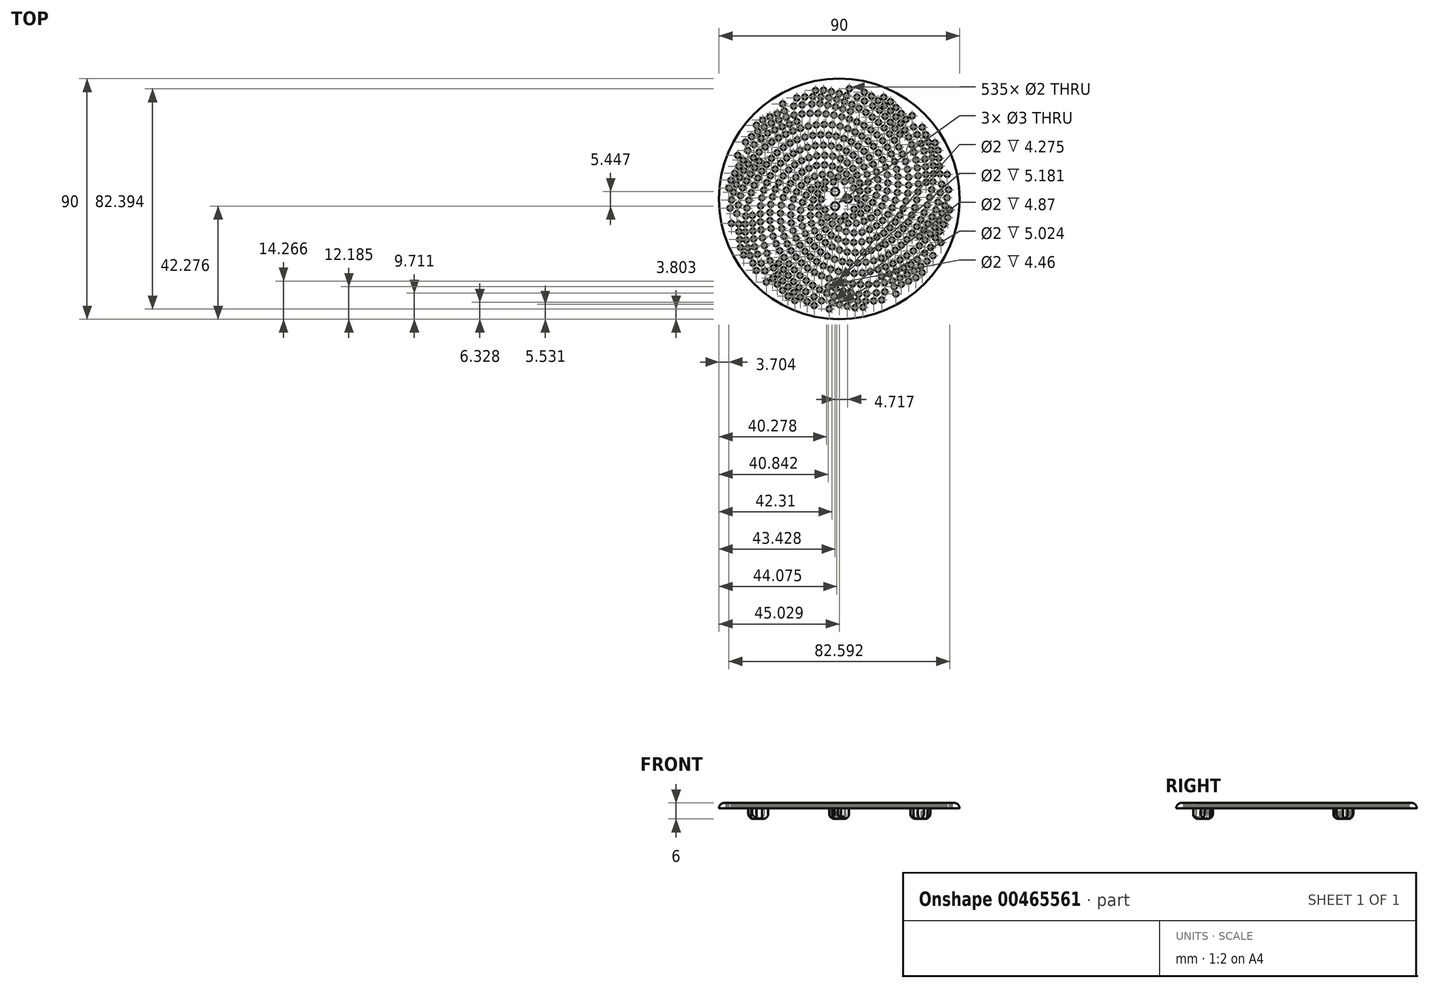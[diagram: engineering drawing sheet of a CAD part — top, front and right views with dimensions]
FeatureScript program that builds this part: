
annotation { "Feature Type Name" : "Feature", "Feature Type Description" : "" }
export const myFeature = defineFeature(function(context is Context, id is Id, definition is map)
    precondition{}
    {
        {
            var Q0;
            Q0=qCreatedBy(makeId("Top.planeOp"),FACE);
            var sketch = newSketch(context, id + "F0", { "sketchPlane" : qUnion([Q0])});
            skCircle(sketch, "E0", {"center": v(0, 0) * mm, "radius": 45 * mm});
            skSolve(sketch);
        }
        {
            var Q0;
            Q0=makeQuery(id+"F0.imprint","IMPRINT",FACE,{"disambiguationData":[TD([[makeQuery(id+"F0.imprint","IMPRINT",EDGE,{"derivedFrom":sQuery(id+"F0.wireOp",EDGE,"E0")}),1.0]])]});
            extrude(context, id + "F1", {"entities" : qUnion([Q0]), "depth" : 2 * mm});
        }
        {
            var Q0;
            Q0=makeQuery(id+"F1.opExtrude","CAP_FACE",FACE,{"disambiguationData":[OSD([sQuery(id+"F0.wireOp",EDGE,"E0")])],"isStart":true});
            var sketch = newSketch(context, id + "F2", { "sketchPlane" : qUnion([Q0])});
            skCircle(sketch, "E1", {"center": v(0, 35) * mm, "radius": 5.25 * mm});
            skCircle(sketch, "E2.1.0", {"center": v(-30.31, -17.5) * mm, "radius": 5.25 * mm});
            skCircle(sketch, "E2.2.0", {"center": v(30.31, -17.5) * mm, "radius": 5.25 * mm});
            skPoint(sketch, "E2.center", {"position": v(0, 0) * mm});
            skSolve(sketch);
        }
        {
            var Q0;
            Q0 = qSketchRegion(id + "F2", true);
            extrude(context, id + "F3", {"entities" : qUnion([Q0]), "operationType" : NewBodyOperationType.REMOVE, "oppositeDirection" : true, "depth" : 1 * mm});
        }
        {
            var Q0;
            Q0=makeQuery(id+"F3.boolean.opBoolean","COPY",FACE,{"derivedFrom":makeQuery(id+"F3.opExtrude","CAP_FACE",FACE,{"disambiguationData":[OSD([sQuery(id+"F2.wireOp",EDGE,"E1")])],"isStart":false})});
            var sketch = newSketch(context, id + "F4", { "sketchPlane" : qUnion([Q0])});
            skCircle(sketch, "E3", {"center": v(0, 35) * mm, "radius": 3.75 * mm});
            skCircle(sketch, "E4.1.0", {"center": v(-30.31, -17.5) * mm, "radius": 3.75 * mm});
            skCircle(sketch, "E4.2.0", {"center": v(30.31, -17.5) * mm, "radius": 3.75 * mm});
            skPoint(sketch, "E4.center", {"position": v(0, 0) * mm});
            skSolve(sketch);
        }
        {
            var Q0;
            Q0=makeQuery(id+"F4.imprint","IMPRINT",FACE,{"disambiguationData":[TD([[makeQuery(id+"F4.imprint","IMPRINT",EDGE,{"derivedFrom":sQuery(id+"F4.wireOp",EDGE,"E3")}),1.0]])]});
            var Q1;
            Q1=makeQuery(id+"F4.imprint","IMPRINT",FACE,{"disambiguationData":[TD([[makeQuery(id+"F4.imprint","IMPRINT",EDGE,{"derivedFrom":sQuery(id+"F4.wireOp",EDGE,"E4.2.0")}),1.0]])]});
            var Q2;
            Q2=makeQuery(id+"F4.imprint","IMPRINT",FACE,{"disambiguationData":[TD([[makeQuery(id+"F4.imprint","IMPRINT",EDGE,{"derivedFrom":sQuery(id+"F4.wireOp",EDGE,"E4.1.0")}),1.0]])]});
            extrude(context, id + "F5", {"entities" : qUnion([Q0, Q1, Q2]), "operationType" : NewBodyOperationType.ADD, "depth" : 5 * mm});
        }
        {
            var Q0;
            Q0=makeQuery(id+"F5.opExtrude","CAP_FACE",FACE,{"disambiguationData":[OSD([sQuery(id+"F4.wireOp",EDGE,"E4.1.0")])],"isStart":false});
            var Q1;
            Q1=makeQuery(id+"F5.opExtrude","CAP_FACE",FACE,{"disambiguationData":[OSD([sQuery(id+"F4.wireOp",EDGE,"E3")])],"isStart":false});
            var Q2;
            Q2=makeQuery(id+"F5.opExtrude","CAP_FACE",FACE,{"disambiguationData":[OSD([sQuery(id+"F4.wireOp",EDGE,"E4.2.0")])],"isStart":false});
            fillet(context, id + "F6", {"entities" : qUnion([Q0, Q1, Q2]), "radius" : 2 * mm, "tangentPropagation" : true, "allowEdgeOverflow" : false});
        }
        {
            var Q0;
            Q0=makeQuery(id+"F1.opExtrude","CAP_EDGE",EDGE,{"disambiguationData":[OSD([sQuery(id+"F0.wireOp",EDGE,"E0")])],"isStart":false});
            fillet(context, id + "F7", {"entities" : qUnion([Q0]), "radius" : 2 * mm, "tangentPropagation" : true, "allowEdgeOverflow" : false});
        }
        {
            var Q0;
            Q0=makeQuery(id+"F1.opExtrude","CAP_FACE",FACE,{"disambiguationData":[OSD([sQuery(id+"F0.wireOp",EDGE,"E0")])],"isStart":false});
            var sketch = newSketch(context, id + "F8", { "sketchPlane" : qUnion([Q0])});
            skCircle(sketch, "E5", {"center": v(0, 0) * mm, "radius": 4.62 * mm, "construction": true});
            skFitSpline(sketch, "E6", {"points": [v(-41.37, -9.4) * mm, v(-31.79, 15.74) * mm, v(-5.3, 27.85) * mm, v(12.82, 19.64) * mm, v(18.16, 6) * mm, v(13.17, -6.11) * mm, v(3.17, -9.08) * mm, v(-2.43, -5.86) * mm, v(-4.4, -1.42) * mm], "startDerivative": vector(4.04, 165.6) * mm, "endDerivative": vector(-19.47, 63.53) * mm, "construction": true});
            skCircle(sketch, "E7", {"center": v(-40.85, -3.42) * mm, "radius": 1 * mm});
            skCircle(sketch, "E8", {"center": v(-37.22, 8.02) * mm, "radius": 1 * mm});
            skCircle(sketch, "E9", {"center": v(-39.48, 2.47) * mm, "radius": 1 * mm});
            skCircle(sketch, "E10", {"center": v(-38.47, 5.3) * mm, "radius": 1 * mm});
            skCircle(sketch, "E11", {"center": v(-40.27, -0.42) * mm, "radius": 1 * mm});
            skCircle(sketch, "E12", {"center": v(-35.74, 10.63) * mm, "radius": 1 * mm});
            skCircle(sketch, "E13", {"center": v(-34.03, 13.1) * mm, "radius": 1 * mm});
            skCircle(sketch, "E14", {"center": v(-32.1, 15.4) * mm, "radius": 1 * mm});
            skCircle(sketch, "E15", {"center": v(-22.72, 22.8) * mm, "radius": 1 * mm});
            skCircle(sketch, "E16", {"center": v(-27.7, 19.46) * mm, "radius": 1 * mm});
            skCircle(sketch, "E17", {"center": v(-25.27, 21.22) * mm, "radius": 1 * mm});
            skCircle(sketch, "E18", {"center": v(-29.98, 17.52) * mm, "radius": 1 * mm});
            skCircle(sketch, "E19", {"center": v(-20.06, 24.2) * mm, "radius": 1 * mm});
            skCircle(sketch, "E20", {"center": v(-17.32, 25.4) * mm, "radius": 1 * mm});
            skCircle(sketch, "E21", {"center": v(-14.49, 26.4) * mm, "radius": 1 * mm});
            skCircle(sketch, "E22", {"center": v(-11.58, 27.16) * mm, "radius": 1 * mm});
            skCircle(sketch, "E23", {"center": v(-8.63, 27.66) * mm, "radius": 1 * mm});
            skCircle(sketch, "E24", {"center": v(-5.63, 27.85) * mm, "radius": 1 * mm});
            skCircle(sketch, "E25", {"center": v(5.91, 25.02) * mm, "radius": 1 * mm});
            skCircle(sketch, "E26", {"center": v(0.31, 27.15) * mm, "radius": 1 * mm});
            skCircle(sketch, "E27", {"center": v(3.18, 26.26) * mm, "radius": 1 * mm});
            skCircle(sketch, "E28", {"center": v(-2.64, 27.69) * mm, "radius": 1 * mm});
            skCircle(sketch, "E29", {"center": v(8.48, 23.46) * mm, "radius": 1 * mm});
            skCircle(sketch, "E30", {"center": v(10.84, 21.61) * mm, "radius": 1 * mm});
            skCircle(sketch, "E31", {"center": v(12.82, 19.64) * mm, "radius": 1 * mm});
            skCircle(sketch, "E32", {"center": v(14.67, 17.28) * mm, "radius": 1 * mm});
            skCircle(sketch, "E33", {"center": v(16.18, 14.68) * mm, "radius": 1 * mm});
            skCircle(sketch, "E34", {"center": v(17.29, 11.9) * mm, "radius": 1 * mm});
            skCircle(sketch, "E35", {"center": v(17.16, 0.1) * mm, "radius": 1 * mm});
            skCircle(sketch, "E36", {"center": v(18.16, 6) * mm, "radius": 1 * mm});
            skCircle(sketch, "E37", {"center": v(17.9, 3.02) * mm, "radius": 1 * mm});
            skCircle(sketch, "E38", {"center": v(17.96, 8.97) * mm, "radius": 1 * mm});
            skCircle(sketch, "E39", {"center": v(15.94, -2.63) * mm, "radius": 1 * mm});
            skCircle(sketch, "E40", {"center": v(14.2, -5.08) * mm, "radius": 1 * mm});
            skCircle(sketch, "E41", {"center": v(6.34, -9.1) * mm, "radius": 1 * mm});
            skCircle(sketch, "E42", {"center": v(3.34, -9.1) * mm, "radius": 1 * mm});
            skCircle(sketch, "E43", {"center": v(9.26, -8.4) * mm, "radius": 1 * mm});
            skCircle(sketch, "E44", {"center": v(11.94, -7.05) * mm, "radius": 1 * mm});
            skCircle(sketch, "E45", {"center": v(0.47, -8.23) * mm, "radius": 1 * mm});
            skCircle(sketch, "E46", {"center": v(-1.94, -6.45) * mm, "radius": 1 * mm});
            skCircle(sketch, "E47.1.1", {"center": v(13.8, 1.32) * mm, "radius": 1 * mm});
            skCircle(sketch, "E47.1.2", {"center": v(-9.92, 23.72) * mm, "radius": 1 * mm});
            skCircle(sketch, "E47.1.3", {"center": v(10.48, -3.64) * mm, "radius": 1 * mm});
            skCircle(sketch, "E47.1.4", {"center": v(7, 19.79) * mm, "radius": 1 * mm});
            skCircle(sketch, "E47.1.5", {"center": v(9.25, 17.82) * mm, "radius": 1 * mm});
            skCircle(sketch, "E47.1.6", {"center": v(-25.34, 15.17) * mm, "radius": 1 * mm});
            skCircle(sketch, "E47.1.7", {"center": v(-34.55, -3.45) * mm, "radius": 1 * mm});
            skCircle(sketch, "E47.1.8", {"center": v(-30.46, 7.79) * mm, "radius": 1 * mm});
            skCircle(sketch, "E47.1.9", {"center": v(4.46, 21.39) * mm, "radius": 1 * mm});
            skCircle(sketch, "E47.1.10", {"center": v(-28.94, 10.38) * mm, "radius": 1 * mm});
            skCircle(sketch, "E47.1.11", {"center": v(-31.04, -26.78) * mm, "radius": 1 * mm});
            skCircle(sketch, "E47.1.12", {"center": v(-34.83, -15.39) * mm, "radius": 1 * mm});
            skCircle(sketch, "E47.1.13", {"center": v(-33.4, -21.2) * mm, "radius": 1 * mm});
            skCircle(sketch, "E47.1.14", {"center": v(-32.33, -24.01) * mm, "radius": 1 * mm});
            skCircle(sketch, "E47.1.15", {"center": v(13.82, 10.17) * mm, "radius": 1 * mm});
            skCircle(sketch, "E47.1.16", {"center": v(-35.16, -12.4) * mm, "radius": 1 * mm});
            skCircle(sketch, "E47.1.17", {"center": v(-35.23, -9.4) * mm, "radius": 1 * mm});
            skCircle(sketch, "E47.1.18", {"center": v(-35.02, -6.41) * mm, "radius": 1 * mm});
            skCircle(sketch, "E47.1.19", {"center": v(-31.78, 5.1) * mm, "radius": 1 * mm});
            skCircle(sketch, "E47.1.20", {"center": v(-3.94, 23.86) * mm, "radius": 1 * mm});
            skCircle(sketch, "E47.1.21", {"center": v(-33.84, -0.54) * mm, "radius": 1 * mm});
            skCircle(sketch, "E47.1.22", {"center": v(-32.92, 2.32) * mm, "radius": 1 * mm});
            skCircle(sketch, "E47.1.23", {"center": v(2.22, -6.35) * mm, "radius": 1 * mm});
            skCircle(sketch, "E47.1.24", {"center": v(12.42, -1.35) * mm, "radius": 1 * mm});
            skCircle(sketch, "E47.1.25", {"center": v(-27.24, 12.85) * mm, "radius": 1 * mm});
            skCircle(sketch, "E47.1.26", {"center": v(-6.93, 23.97) * mm, "radius": 1 * mm});
            skCircle(sketch, "E47.1.27", {"center": v(-18.4, 20.85) * mm, "radius": 1 * mm});
            skCircle(sketch, "E47.1.28", {"center": v(14.44, 7.24) * mm, "radius": 1 * mm});
            skCircle(sketch, "E47.1.29", {"center": v(14.48, 4.24) * mm, "radius": 1 * mm});
            skCircle(sketch, "E47.1.30", {"center": v(12.7, 12.96) * mm, "radius": 1 * mm});
            skCircle(sketch, "E47.1.31", {"center": v(1.71, 22.6) * mm, "radius": 1 * mm});
            skCircle(sketch, "E47.1.32", {"center": v(-34.23, -18.33) * mm, "radius": 1 * mm});
            skCircle(sketch, "E47.1.33", {"center": v(8.06, -5.4) * mm, "radius": 1 * mm});
            skCircle(sketch, "E47.1.34", {"center": v(-15.7, 22.15) * mm, "radius": 1 * mm});
            skCircle(sketch, "E47.1.35", {"center": v(-1.17, 23.43) * mm, "radius": 1 * mm});
            skCircle(sketch, "E47.1.36", {"center": v(11.16, 15.53) * mm, "radius": 1 * mm});
            skCircle(sketch, "E47.1.37", {"center": v(-23.24, 17.3) * mm, "radius": 1 * mm});
            skCircle(sketch, "E47.1.38", {"center": v(-12.86, 23.11) * mm, "radius": 1 * mm});
            skCircle(sketch, "E47.1.39", {"center": v(5.22, -6.38) * mm, "radius": 1 * mm});
            skCircle(sketch, "E47.1.40", {"center": v(-20.93, 19.22) * mm, "radius": 1 * mm});
            skCircle(sketch, "E47.2.1", {"center": v(10.4, 9.18) * mm, "radius": 1 * mm});
            skCircle(sketch, "E47.2.2", {"center": v(-21.97, 13.35) * mm, "radius": 1 * mm});
            skCircle(sketch, "E47.2.3", {"center": v(10.62, 3.22) * mm, "radius": 1 * mm});
            skCircle(sketch, "E47.2.4", {"center": v(-5.97, 20.12) * mm, "radius": 1 * mm});
            skCircle(sketch, "E47.2.5", {"center": v(-2.99, 19.85) * mm, "radius": 1 * mm});
            skCircle(sketch, "E47.2.6", {"center": v(-29.42, -2.62) * mm, "radius": 1 * mm});
            skCircle(sketch, "E47.2.7", {"center": v(-25.93, -23.1) * mm, "radius": 1 * mm});
            skCircle(sketch, "E47.2.8", {"center": v(-29.22, -11.6) * mm, "radius": 1 * mm});
            skCircle(sketch, "E47.2.9", {"center": v(-8.97, 19.92) * mm, "radius": 1 * mm});
            skCircle(sketch, "E47.2.10", {"center": v(-29.52, -8.62) * mm, "radius": 1 * mm});
            skCircle(sketch, "E47.2.11", {"center": v(-9.37, -39.9) * mm, "radius": 1 * mm});
            skCircle(sketch, "E47.2.12", {"center": v(-19.13, -32.92) * mm, "radius": 1 * mm});
            skCircle(sketch, "E47.2.13", {"center": v(-14.55, -36.79) * mm, "radius": 1 * mm});
            skCircle(sketch, "E47.2.14", {"center": v(-12.04, -38.43) * mm, "radius": 1 * mm});
            skCircle(sketch, "E47.2.15", {"center": v(5.2, 16.35) * mm, "radius": 1 * mm});
            skCircle(sketch, "E47.2.16", {"center": v(-21.15, -30.7) * mm, "radius": 1 * mm});
            skCircle(sketch, "E47.2.17", {"center": v(-22.97, -28.32) * mm, "radius": 1 * mm});
            skCircle(sketch, "E47.2.18", {"center": v(-24.56, -25.77) * mm, "radius": 1 * mm});
            skCircle(sketch, "E47.2.19", {"center": v(-28.7, -14.56) * mm, "radius": 1 * mm});
            skCircle(sketch, "E47.2.20", {"center": v(-17.2, 16.99) * mm, "radius": 1 * mm});
            skCircle(sketch, "E47.2.21", {"center": v(-27.06, -20.33) * mm, "radius": 1 * mm});
            skCircle(sketch, "E47.2.22", {"center": v(-28, -17.47) * mm, "radius": 1 * mm});
            skCircle(sketch, "E47.2.23", {"center": v(5.53, -3.83) * mm, "radius": 1 * mm});
            skCircle(sketch, "E47.2.24", {"center": v(10.84, 6.21) * mm, "radius": 1 * mm});
            skCircle(sketch, "E47.2.25", {"center": v(-29.59, -5.62) * mm, "radius": 1 * mm});
            skCircle(sketch, "E47.2.26", {"center": v(-19.7, 15.31) * mm, "radius": 1 * mm});
            skCircle(sketch, "E47.2.27", {"center": v(-27.15, 6.05) * mm, "radius": 1 * mm});
            skCircle(sketch, "E47.2.28", {"center": v(7.43, 14.35) * mm, "radius": 1 * mm});
            skCircle(sketch, "E47.2.29", {"center": v(9.22, 11.94) * mm, "radius": 1 * mm});
            skCircle(sketch, "E47.2.30", {"center": v(2.66, 17.95) * mm, "radius": 1 * mm});
            skCircle(sketch, "E47.2.31", {"center": v(-11.9, 19.3) * mm, "radius": 1 * mm});
            skCircle(sketch, "E47.2.32", {"center": v(-16.92, -34.95) * mm, "radius": 1 * mm});
            skCircle(sketch, "E47.2.33", {"center": v(9.7, 0.37) * mm, "radius": 1 * mm});
            skCircle(sketch, "E47.2.34", {"center": v(-25.73, 8.69) * mm, "radius": 1 * mm});
            skCircle(sketch, "E47.2.35", {"center": v(-14.72, 18.26) * mm, "radius": 1 * mm});
            skCircle(sketch, "E47.2.36", {"center": v(-0.1, 19.13) * mm, "radius": 1 * mm});
            skCircle(sketch, "E47.2.37", {"center": v(-28.97, 0.34) * mm, "radius": 1 * mm});
            skCircle(sketch, "E47.2.38", {"center": v(-23.99, 11.14) * mm, "radius": 1 * mm});
            skCircle(sketch, "E47.2.39", {"center": v(7.98, -2.1) * mm, "radius": 1 * mm});
            skCircle(sketch, "E47.2.40", {"center": v(-28.23, 3.25) * mm, "radius": 1 * mm});
            skCircle(sketch, "E47.3.1", {"center": v(3.01, 13.53) * mm, "radius": 1 * mm});
            skCircle(sketch, "E47.3.2", {"center": v(-25.62, -2.1) * mm, "radius": 1 * mm});
            skCircle(sketch, "E47.3.3", {"center": v(6.7, 8.85) * mm, "radius": 1 * mm});
            skCircle(sketch, "E47.3.4", {"center": v(-16.66, 12.76) * mm, "radius": 1 * mm});
            skCircle(sketch, "E47.3.5", {"center": v(-14.08, 14.3) * mm, "radius": 1 * mm});
            skCircle(sketch, "E47.3.6", {"center": v(-22.26, -19.41) * mm, "radius": 1 * mm});
            skCircle(sketch, "E47.3.7", {"center": v(-7.4, -33.93) * mm, "radius": 1 * mm});
            skCircle(sketch, "E47.3.8", {"center": v(-16.82, -26.56) * mm, "radius": 1 * mm});
            skCircle(sketch, "E47.3.9", {"center": v(-18.96, 10.85) * mm, "radius": 1 * mm});
            skCircle(sketch, "E47.3.10", {"center": v(-18.81, -24.32) * mm, "radius": 1 * mm});
            skCircle(sketch, "E47.3.11", {"center": v(15.88, -37.8) * mm, "radius": 1 * mm});
            skCircle(sketch, "E47.3.12", {"center": v(3.87, -37.88) * mm, "radius": 1 * mm});
            skCircle(sketch, "E47.3.13", {"center": v(9.85, -38.31) * mm, "radius": 1 * mm});
            skCircle(sketch, "E47.3.14", {"center": v(12.85, -38.17) * mm, "radius": 1 * mm});
            skCircle(sketch, "E47.3.15", {"center": v(-5.4, 16.28) * mm, "radius": 1 * mm});
            skCircle(sketch, "E47.3.16", {"center": v(0.93, -37.27) * mm, "radius": 1 * mm});
            skCircle(sketch, "E47.3.17", {"center": v(-1.94, -36.4) * mm, "radius": 1 * mm});
            skCircle(sketch, "E47.3.18", {"center": v(-4.72, -35.29) * mm, "radius": 1 * mm});
            skCircle(sketch, "E47.3.19", {"center": v(-14.67, -28.65) * mm, "radius": 1 * mm});
            skCircle(sketch, "E47.3.20", {"center": v(-23.9, 3.63) * mm, "radius": 1 * mm});
            skCircle(sketch, "E47.3.21", {"center": v(-9.95, -32.35) * mm, "radius": 1 * mm});
            skCircle(sketch, "E47.3.22", {"center": v(-12.38, -30.59) * mm, "radius": 1 * mm});
            skCircle(sketch, "E47.3.23", {"center": v(6.73, 0.15) * mm, "radius": 1 * mm});
            skCircle(sketch, "E47.3.24", {"center": v(5.12, 11.4) * mm, "radius": 1 * mm});
            skCircle(sketch, "E47.3.25", {"center": v(-20.63, -21.94) * mm, "radius": 1 * mm});
            skCircle(sketch, "E47.3.26", {"center": v(-24.94, 0.81) * mm, "radius": 1 * mm});
            skCircle(sketch, "E47.3.27", {"center": v(-25.52, -11.06) * mm, "radius": 1 * mm});
            skCircle(sketch, "E47.3.28", {"center": v(-2.42, 15.97) * mm, "radius": 1 * mm});
            skCircle(sketch, "E47.3.29", {"center": v(0.44, 15.08) * mm, "radius": 1 * mm});
            skCircle(sketch, "E47.3.30", {"center": v(-8.4, 16.08) * mm, "radius": 1 * mm});
            skCircle(sketch, "E47.3.31", {"center": v(-20.97, 8.61) * mm, "radius": 1 * mm});
            skCircle(sketch, "E47.3.32", {"center": v(6.85, -38.22) * mm, "radius": 1 * mm});
            skCircle(sketch, "E47.3.33", {"center": v(7.63, 6) * mm, "radius": 1 * mm});
            skCircle(sketch, "E47.3.34", {"center": v(-25.92, -8.1) * mm, "radius": 1 * mm});
            skCircle(sketch, "E47.3.35", {"center": v(-22.64, 6.12) * mm, "radius": 1 * mm});
            skCircle(sketch, "E47.3.36", {"center": v(-11.32, 15.42) * mm, "radius": 1 * mm});
            skCircle(sketch, "E47.3.37", {"center": v(-23.64, -16.75) * mm, "radius": 1 * mm});
            skCircle(sketch, "E47.3.38", {"center": v(-25.95, -5.1) * mm, "radius": 1 * mm});
            skCircle(sketch, "E47.3.39", {"center": v(7.68, 3) * mm, "radius": 1 * mm});
            skCircle(sketch, "E47.3.40", {"center": v(-24.75, -13.96) * mm, "radius": 1 * mm});
            skCircle(sketch, "E47.4.1", {"center": v(-5.52, 12.72) * mm, "radius": 1 * mm});
            skCircle(sketch, "E47.4.2", {"center": v(-19.49, -16.77) * mm, "radius": 1 * mm});
            skCircle(sketch, "E47.4.3", {"center": v(0.22, 11.1) * mm, "radius": 1 * mm});
            skCircle(sketch, "E47.4.4", {"center": v(-20.98, 0.54) * mm, "radius": 1 * mm});
            skCircle(sketch, "E47.4.5", {"center": v(-19.8, 3.3) * mm, "radius": 1 * mm});
            skCircle(sketch, "E47.4.6", {"center": v(-6.6, -28.79) * mm, "radius": 1 * mm});
            skCircle(sketch, "E47.4.7", {"center": v(13.96, -31.8) * mm, "radius": 1 * mm});
            skCircle(sketch, "E47.4.8", {"center": v(2, -31.37) * mm, "radius": 1 * mm});
            skCircle(sketch, "E47.4.9", {"center": v(-21.72, -2.37) * mm, "radius": 1 * mm});
            skCircle(sketch, "E47.4.10", {"center": v(-0.92, -30.73) * mm, "radius": 1 * mm});
            skCircle(sketch, "E47.4.11", {"center": v(35.06, -21.24) * mm, "radius": 1 * mm});
            skCircle(sketch, "E47.4.12", {"center": v(25.4, -28.37) * mm, "radius": 1 * mm});
            skCircle(sketch, "E47.4.13", {"center": v(30.5, -25.2) * mm, "radius": 1 * mm});
            skCircle(sketch, "E47.4.14", {"center": v(32.83, -23.33) * mm, "radius": 1 * mm});
            skCircle(sketch, "E47.4.15", {"center": v(-13.94, 10) * mm, "radius": 1 * mm});
            skCircle(sketch, "E47.4.16", {"center": v(22.66, -29.6) * mm, "radius": 1 * mm});
            skCircle(sketch, "E47.4.17", {"center": v(19.83, -30.6) * mm, "radius": 1 * mm});
            skCircle(sketch, "E47.4.18", {"center": v(16.92, -31.33) * mm, "radius": 1 * mm});
            skCircle(sketch, "E47.4.19", {"center": v(4.98, -31.8) * mm, "radius": 1 * mm});
            skCircle(sketch, "E47.4.20", {"center": v(-21.47, -11.12) * mm, "radius": 1 * mm});
            skCircle(sketch, "E47.4.21", {"center": v(10.97, -32.02) * mm, "radius": 1 * mm});
            skCircle(sketch, "E47.4.22", {"center": v(7.97, -32.02) * mm, "radius": 1 * mm});
            skCircle(sketch, "E47.4.23", {"center": v(5.36, 4.08) * mm, "radius": 1 * mm});
            skCircle(sketch, "E47.4.24", {"center": v(-2.56, 12.23) * mm, "radius": 1 * mm});
            skCircle(sketch, "E47.4.25", {"center": v(-3.8, -29.87) * mm, "radius": 1 * mm});
            skCircle(sketch, "E47.4.26", {"center": v(-20.65, -14) * mm, "radius": 1 * mm});
            skCircle(sketch, "E47.4.27", {"center": v(-14.14, -23.95) * mm, "radius": 1 * mm});
            skCircle(sketch, "E47.4.28", {"center": v(-11.35, 11.5) * mm, "radius": 1 * mm});
            skCircle(sketch, "E47.4.29", {"center": v(-8.5, 12.46) * mm, "radius": 1 * mm});
            skCircle(sketch, "E47.4.30", {"center": v(-16.25, 8.08) * mm, "radius": 1 * mm});
            skCircle(sketch, "E47.4.31", {"center": v(-22.02, -5.36) * mm, "radius": 1 * mm});
            skCircle(sketch, "E47.4.32", {"center": v(28, -26.9) * mm, "radius": 1 * mm});
            skCircle(sketch, "E47.4.33", {"center": v(2.65, 9.33) * mm, "radius": 1 * mm});
            skCircle(sketch, "E47.4.34", {"center": v(-16.21, -21.78) * mm, "radius": 1 * mm});
            skCircle(sketch, "E47.4.35", {"center": v(-21.92, -8.35) * mm, "radius": 1 * mm});
            skCircle(sketch, "E47.4.36", {"center": v(-18.22, 5.82) * mm, "radius": 1 * mm});
            skCircle(sketch, "E47.4.37", {"center": v(-9.28, -27.45) * mm, "radius": 1 * mm});
            skCircle(sketch, "E47.4.38", {"center": v(-18, -19.37) * mm, "radius": 1 * mm});
            skCircle(sketch, "E47.4.39", {"center": v(4.46, 6.94) * mm, "radius": 1 * mm});
            skCircle(sketch, "E47.4.40", {"center": v(-11.82, -25.84) * mm, "radius": 1 * mm});
            skCircle(sketch, "E47.5.1", {"center": v(-11.94, 7.05) * mm, "radius": 1 * mm});
            skCircle(sketch, "E47.5.2", {"center": v(-5.91, -25.02) * mm, "radius": 1 * mm});
            skCircle(sketch, "E47.5.3", {"center": v(-6.34, 9.1) * mm, "radius": 1 * mm});
            skCircle(sketch, "E47.5.4", {"center": v(-17.29, -11.9) * mm, "radius": 1 * mm});
            skCircle(sketch, "E47.5.5", {"center": v(-17.96, -8.97) * mm, "radius": 1 * mm});
            skCircle(sketch, "E47.5.6", {"center": v(11.58, -27.16) * mm, "radius": 1 * mm});
            skCircle(sketch, "E47.5.7", {"center": v(29.98, -17.52) * mm, "radius": 1 * mm});
            skCircle(sketch, "E47.5.8", {"center": v(20.06, -24.2) * mm, "radius": 1 * mm});
            skCircle(sketch, "E47.5.9", {"center": v(-16.18, -14.68) * mm, "radius": 1 * mm});
            skCircle(sketch, "E47.5.10", {"center": v(17.32, -25.4) * mm, "radius": 1 * mm});
            skCircle(sketch, "E47.5.11", {"center": v(40.85, 3.42) * mm, "radius": 1 * mm});
            skCircle(sketch, "E47.5.12", {"center": v(37.22, -8.02) * mm, "radius": 1 * mm});
            skCircle(sketch, "E47.5.13", {"center": v(39.48, -2.47) * mm, "radius": 1 * mm});
            skCircle(sketch, "E47.5.14", {"center": v(40.27, 0.42) * mm, "radius": 1 * mm});
            skCircle(sketch, "E47.5.15", {"center": v(-17.16, -0.1) * mm, "radius": 1 * mm});
            skCircle(sketch, "E47.5.16", {"center": v(35.74, -10.63) * mm, "radius": 1 * mm});
            skCircle(sketch, "E47.5.17", {"center": v(34.03, -13.1) * mm, "radius": 1 * mm});
            skCircle(sketch, "E47.5.18", {"center": v(32.1, -15.4) * mm, "radius": 1 * mm});
            skCircle(sketch, "E47.5.19", {"center": v(22.72, -22.8) * mm, "radius": 1 * mm});
            skCircle(sketch, "E47.5.20", {"center": v(-10.84, -21.61) * mm, "radius": 1 * mm});
            skCircle(sketch, "E47.5.21", {"center": v(27.7, -19.46) * mm, "radius": 1 * mm});
            skCircle(sketch, "E47.5.22", {"center": v(25.27, -21.22) * mm, "radius": 1 * mm});
            skCircle(sketch, "E47.5.23", {"center": v(1.94, 6.45) * mm, "radius": 1 * mm});
            skCircle(sketch, "E47.5.24", {"center": v(-9.26, 8.4) * mm, "radius": 1 * mm});
            skCircle(sketch, "E47.5.25", {"center": v(14.49, -26.4) * mm, "radius": 1 * mm});
            skCircle(sketch, "E47.5.26", {"center": v(-8.48, -23.46) * mm, "radius": 1 * mm});
            skCircle(sketch, "E47.5.27", {"center": v(2.64, -27.69) * mm, "radius": 1 * mm});
            skCircle(sketch, "E47.5.28", {"center": v(-15.94, 2.63) * mm, "radius": 1 * mm});
            skCircle(sketch, "E47.5.29", {"center": v(-14.2, 5.08) * mm, "radius": 1 * mm});
            skCircle(sketch, "E47.5.30", {"center": v(-17.9, -3.02) * mm, "radius": 1 * mm});
            skCircle(sketch, "E47.5.31", {"center": v(-14.67, -17.28) * mm, "radius": 1 * mm});
            skCircle(sketch, "E47.5.32", {"center": v(38.47, -5.3) * mm, "radius": 1 * mm});
            skCircle(sketch, "E47.5.33", {"center": v(-3.34, 9.1) * mm, "radius": 1 * mm});
            skCircle(sketch, "E47.5.34", {"center": v(-0.31, -27.15) * mm, "radius": 1 * mm});
            skCircle(sketch, "E47.5.35", {"center": v(-12.82, -19.64) * mm, "radius": 1 * mm});
            skCircle(sketch, "E47.5.36", {"center": v(-18.16, -6) * mm, "radius": 1 * mm});
            skCircle(sketch, "E47.5.37", {"center": v(8.63, -27.66) * mm, "radius": 1 * mm});
            skCircle(sketch, "E47.5.38", {"center": v(-3.18, -26.26) * mm, "radius": 1 * mm});
            skCircle(sketch, "E47.5.39", {"center": v(-0.47, 8.23) * mm, "radius": 1 * mm});
            skCircle(sketch, "E47.5.40", {"center": v(5.63, -27.85) * mm, "radius": 1 * mm});
            skCircle(sketch, "E47.6.1", {"center": v(-13.8, -1.32) * mm, "radius": 1 * mm});
            skCircle(sketch, "E47.6.2", {"center": v(9.92, -23.72) * mm, "radius": 1 * mm});
            skCircle(sketch, "E47.6.3", {"center": v(-10.48, 3.64) * mm, "radius": 1 * mm});
            skCircle(sketch, "E47.6.4", {"center": v(-7, -19.79) * mm, "radius": 1 * mm});
            skCircle(sketch, "E47.6.5", {"center": v(-9.25, -17.82) * mm, "radius": 1 * mm});
            skCircle(sketch, "E47.6.6", {"center": v(25.34, -15.17) * mm, "radius": 1 * mm});
            skCircle(sketch, "E47.6.7", {"center": v(34.55, 3.45) * mm, "radius": 1 * mm});
            skCircle(sketch, "E47.6.8", {"center": v(30.46, -7.79) * mm, "radius": 1 * mm});
            skCircle(sketch, "E47.6.9", {"center": v(-4.46, -21.39) * mm, "radius": 1 * mm});
            skCircle(sketch, "E47.6.10", {"center": v(28.94, -10.38) * mm, "radius": 1 * mm});
            skCircle(sketch, "E47.6.11", {"center": v(31.04, 26.78) * mm, "radius": 1 * mm});
            skCircle(sketch, "E47.6.12", {"center": v(34.83, 15.39) * mm, "radius": 1 * mm});
            skCircle(sketch, "E47.6.13", {"center": v(33.4, 21.2) * mm, "radius": 1 * mm});
            skCircle(sketch, "E47.6.14", {"center": v(32.33, 24.01) * mm, "radius": 1 * mm});
            skCircle(sketch, "E47.6.15", {"center": v(-13.82, -10.17) * mm, "radius": 1 * mm});
            skCircle(sketch, "E47.6.16", {"center": v(35.16, 12.4) * mm, "radius": 1 * mm});
            skCircle(sketch, "E47.6.17", {"center": v(35.23, 9.4) * mm, "radius": 1 * mm});
            skCircle(sketch, "E47.6.18", {"center": v(35.02, 6.41) * mm, "radius": 1 * mm});
            skCircle(sketch, "E47.6.19", {"center": v(31.78, -5.1) * mm, "radius": 1 * mm});
            skCircle(sketch, "E47.6.20", {"center": v(3.94, -23.86) * mm, "radius": 1 * mm});
            skCircle(sketch, "E47.6.21", {"center": v(33.84, 0.54) * mm, "radius": 1 * mm});
            skCircle(sketch, "E47.6.22", {"center": v(32.92, -2.32) * mm, "radius": 1 * mm});
            skCircle(sketch, "E47.6.23", {"center": v(-2.22, 6.35) * mm, "radius": 1 * mm});
            skCircle(sketch, "E47.6.24", {"center": v(-12.42, 1.35) * mm, "radius": 1 * mm});
            skCircle(sketch, "E47.6.25", {"center": v(27.24, -12.85) * mm, "radius": 1 * mm});
            skCircle(sketch, "E47.6.26", {"center": v(6.93, -23.97) * mm, "radius": 1 * mm});
            skCircle(sketch, "E47.6.27", {"center": v(18.4, -20.85) * mm, "radius": 1 * mm});
            skCircle(sketch, "E47.6.28", {"center": v(-14.44, -7.24) * mm, "radius": 1 * mm});
            skCircle(sketch, "E47.6.29", {"center": v(-14.48, -4.24) * mm, "radius": 1 * mm});
            skCircle(sketch, "E47.6.30", {"center": v(-12.7, -12.96) * mm, "radius": 1 * mm});
            skCircle(sketch, "E47.6.31", {"center": v(-1.71, -22.6) * mm, "radius": 1 * mm});
            skCircle(sketch, "E47.6.32", {"center": v(34.23, 18.33) * mm, "radius": 1 * mm});
            skCircle(sketch, "E47.6.33", {"center": v(-8.06, 5.4) * mm, "radius": 1 * mm});
            skCircle(sketch, "E47.6.34", {"center": v(15.7, -22.15) * mm, "radius": 1 * mm});
            skCircle(sketch, "E47.6.35", {"center": v(1.17, -23.43) * mm, "radius": 1 * mm});
            skCircle(sketch, "E47.6.36", {"center": v(-11.16, -15.53) * mm, "radius": 1 * mm});
            skCircle(sketch, "E47.6.37", {"center": v(23.24, -17.3) * mm, "radius": 1 * mm});
            skCircle(sketch, "E47.6.38", {"center": v(12.86, -23.11) * mm, "radius": 1 * mm});
            skCircle(sketch, "E47.6.39", {"center": v(-5.22, 6.38) * mm, "radius": 1 * mm});
            skCircle(sketch, "E47.6.40", {"center": v(20.93, -19.22) * mm, "radius": 1 * mm});
            skCircle(sketch, "E47.7.1", {"center": v(-10.4, -9.18) * mm, "radius": 1 * mm});
            skCircle(sketch, "E47.7.2", {"center": v(21.97, -13.35) * mm, "radius": 1 * mm});
            skCircle(sketch, "E47.7.3", {"center": v(-10.62, -3.22) * mm, "radius": 1 * mm});
            skCircle(sketch, "E47.7.4", {"center": v(5.97, -20.12) * mm, "radius": 1 * mm});
            skCircle(sketch, "E47.7.5", {"center": v(2.99, -19.85) * mm, "radius": 1 * mm});
            skCircle(sketch, "E47.7.6", {"center": v(29.42, 2.62) * mm, "radius": 1 * mm});
            skCircle(sketch, "E47.7.7", {"center": v(25.93, 23.1) * mm, "radius": 1 * mm});
            skCircle(sketch, "E47.7.8", {"center": v(29.22, 11.6) * mm, "radius": 1 * mm});
            skCircle(sketch, "E47.7.9", {"center": v(8.97, -19.92) * mm, "radius": 1 * mm});
            skCircle(sketch, "E47.7.10", {"center": v(29.52, 8.62) * mm, "radius": 1 * mm});
            skCircle(sketch, "E47.7.11", {"center": v(9.37, 39.9) * mm, "radius": 1 * mm});
            skCircle(sketch, "E47.7.12", {"center": v(19.13, 32.92) * mm, "radius": 1 * mm});
            skCircle(sketch, "E47.7.13", {"center": v(14.55, 36.79) * mm, "radius": 1 * mm});
            skCircle(sketch, "E47.7.14", {"center": v(12.04, 38.43) * mm, "radius": 1 * mm});
            skCircle(sketch, "E47.7.15", {"center": v(-5.2, -16.35) * mm, "radius": 1 * mm});
            skCircle(sketch, "E47.7.16", {"center": v(21.15, 30.7) * mm, "radius": 1 * mm});
            skCircle(sketch, "E47.7.17", {"center": v(22.97, 28.32) * mm, "radius": 1 * mm});
            skCircle(sketch, "E47.7.18", {"center": v(24.56, 25.77) * mm, "radius": 1 * mm});
            skCircle(sketch, "E47.7.19", {"center": v(28.7, 14.56) * mm, "radius": 1 * mm});
            skCircle(sketch, "E47.7.20", {"center": v(17.2, -16.99) * mm, "radius": 1 * mm});
            skCircle(sketch, "E47.7.21", {"center": v(27.06, 20.33) * mm, "radius": 1 * mm});
            skCircle(sketch, "E47.7.22", {"center": v(28, 17.47) * mm, "radius": 1 * mm});
            skCircle(sketch, "E47.7.23", {"center": v(-5.53, 3.83) * mm, "radius": 1 * mm});
            skCircle(sketch, "E47.7.24", {"center": v(-10.84, -6.21) * mm, "radius": 1 * mm});
            skCircle(sketch, "E47.7.25", {"center": v(29.59, 5.62) * mm, "radius": 1 * mm});
            skCircle(sketch, "E47.7.26", {"center": v(19.7, -15.31) * mm, "radius": 1 * mm});
            skCircle(sketch, "E47.7.27", {"center": v(27.15, -6.05) * mm, "radius": 1 * mm});
            skCircle(sketch, "E47.7.28", {"center": v(-7.43, -14.35) * mm, "radius": 1 * mm});
            skCircle(sketch, "E47.7.29", {"center": v(-9.22, -11.94) * mm, "radius": 1 * mm});
            skCircle(sketch, "E47.7.30", {"center": v(-2.66, -17.95) * mm, "radius": 1 * mm});
            skCircle(sketch, "E47.7.31", {"center": v(11.9, -19.3) * mm, "radius": 1 * mm});
            skCircle(sketch, "E47.7.32", {"center": v(16.92, 34.95) * mm, "radius": 1 * mm});
            skCircle(sketch, "E47.7.33", {"center": v(-9.7, -0.37) * mm, "radius": 1 * mm});
            skCircle(sketch, "E47.7.34", {"center": v(25.73, -8.69) * mm, "radius": 1 * mm});
            skCircle(sketch, "E47.7.35", {"center": v(14.72, -18.26) * mm, "radius": 1 * mm});
            skCircle(sketch, "E47.7.36", {"center": v(0.1, -19.13) * mm, "radius": 1 * mm});
            skCircle(sketch, "E47.7.37", {"center": v(28.97, -0.34) * mm, "radius": 1 * mm});
            skCircle(sketch, "E47.7.38", {"center": v(23.99, -11.14) * mm, "radius": 1 * mm});
            skCircle(sketch, "E47.7.39", {"center": v(-7.98, 2.1) * mm, "radius": 1 * mm});
            skCircle(sketch, "E47.7.40", {"center": v(28.23, -3.25) * mm, "radius": 1 * mm});
            skCircle(sketch, "E47.8.1", {"center": v(-3.01, -13.53) * mm, "radius": 1 * mm});
            skCircle(sketch, "E47.8.2", {"center": v(25.62, 2.1) * mm, "radius": 1 * mm});
            skCircle(sketch, "E47.8.3", {"center": v(-6.7, -8.85) * mm, "radius": 1 * mm});
            skCircle(sketch, "E47.8.4", {"center": v(16.66, -12.76) * mm, "radius": 1 * mm});
            skCircle(sketch, "E47.8.5", {"center": v(14.08, -14.3) * mm, "radius": 1 * mm});
            skCircle(sketch, "E47.8.6", {"center": v(22.26, 19.41) * mm, "radius": 1 * mm});
            skCircle(sketch, "E47.8.7", {"center": v(7.4, 33.93) * mm, "radius": 1 * mm});
            skCircle(sketch, "E47.8.8", {"center": v(16.82, 26.56) * mm, "radius": 1 * mm});
            skCircle(sketch, "E47.8.9", {"center": v(18.96, -10.85) * mm, "radius": 1 * mm});
            skCircle(sketch, "E47.8.10", {"center": v(18.81, 24.32) * mm, "radius": 1 * mm});
            skCircle(sketch, "E47.8.11", {"center": v(-15.88, 37.8) * mm, "radius": 1 * mm});
            skCircle(sketch, "E47.8.12", {"center": v(-3.87, 37.88) * mm, "radius": 1 * mm});
            skCircle(sketch, "E47.8.13", {"center": v(-9.85, 38.31) * mm, "radius": 1 * mm});
            skCircle(sketch, "E47.8.14", {"center": v(-12.85, 38.17) * mm, "radius": 1 * mm});
            skCircle(sketch, "E47.8.15", {"center": v(5.4, -16.28) * mm, "radius": 1 * mm});
            skCircle(sketch, "E47.8.16", {"center": v(-0.93, 37.27) * mm, "radius": 1 * mm});
            skCircle(sketch, "E47.8.17", {"center": v(1.94, 36.4) * mm, "radius": 1 * mm});
            skCircle(sketch, "E47.8.18", {"center": v(4.72, 35.29) * mm, "radius": 1 * mm});
            skCircle(sketch, "E47.8.19", {"center": v(14.67, 28.65) * mm, "radius": 1 * mm});
            skCircle(sketch, "E47.8.20", {"center": v(23.9, -3.63) * mm, "radius": 1 * mm});
            skCircle(sketch, "E47.8.21", {"center": v(9.95, 32.35) * mm, "radius": 1 * mm});
            skCircle(sketch, "E47.8.22", {"center": v(12.38, 30.59) * mm, "radius": 1 * mm});
            skCircle(sketch, "E47.8.23", {"center": v(-6.73, -0.15) * mm, "radius": 1 * mm});
            skCircle(sketch, "E47.8.24", {"center": v(-5.12, -11.4) * mm, "radius": 1 * mm});
            skCircle(sketch, "E47.8.25", {"center": v(20.63, 21.94) * mm, "radius": 1 * mm});
            skCircle(sketch, "E47.8.26", {"center": v(24.94, -0.81) * mm, "radius": 1 * mm});
            skCircle(sketch, "E47.8.27", {"center": v(25.52, 11.06) * mm, "radius": 1 * mm});
            skCircle(sketch, "E47.8.28", {"center": v(2.42, -15.97) * mm, "radius": 1 * mm});
            skCircle(sketch, "E47.8.29", {"center": v(-0.44, -15.08) * mm, "radius": 1 * mm});
            skCircle(sketch, "E47.8.30", {"center": v(8.4, -16.08) * mm, "radius": 1 * mm});
            skCircle(sketch, "E47.8.31", {"center": v(20.97, -8.61) * mm, "radius": 1 * mm});
            skCircle(sketch, "E47.8.32", {"center": v(-6.85, 38.22) * mm, "radius": 1 * mm});
            skCircle(sketch, "E47.8.33", {"center": v(-7.63, -6) * mm, "radius": 1 * mm});
            skCircle(sketch, "E47.8.34", {"center": v(25.92, 8.1) * mm, "radius": 1 * mm});
            skCircle(sketch, "E47.8.35", {"center": v(22.64, -6.12) * mm, "radius": 1 * mm});
            skCircle(sketch, "E47.8.36", {"center": v(11.32, -15.42) * mm, "radius": 1 * mm});
            skCircle(sketch, "E47.8.37", {"center": v(23.64, 16.75) * mm, "radius": 1 * mm});
            skCircle(sketch, "E47.8.38", {"center": v(25.95, 5.1) * mm, "radius": 1 * mm});
            skCircle(sketch, "E47.8.39", {"center": v(-7.68, -3) * mm, "radius": 1 * mm});
            skCircle(sketch, "E47.8.40", {"center": v(24.75, 13.96) * mm, "radius": 1 * mm});
            skCircle(sketch, "E47.9.1", {"center": v(5.52, -12.72) * mm, "radius": 1 * mm});
            skCircle(sketch, "E47.9.2", {"center": v(19.49, 16.77) * mm, "radius": 1 * mm});
            skCircle(sketch, "E47.9.3", {"center": v(-0.22, -11.1) * mm, "radius": 1 * mm});
            skCircle(sketch, "E47.9.4", {"center": v(20.98, -0.54) * mm, "radius": 1 * mm});
            skCircle(sketch, "E47.9.5", {"center": v(19.8, -3.3) * mm, "radius": 1 * mm});
            skCircle(sketch, "E47.9.6", {"center": v(6.6, 28.79) * mm, "radius": 1 * mm});
            skCircle(sketch, "E47.9.7", {"center": v(-13.96, 31.8) * mm, "radius": 1 * mm});
            skCircle(sketch, "E47.9.8", {"center": v(-2, 31.37) * mm, "radius": 1 * mm});
            skCircle(sketch, "E47.9.9", {"center": v(21.72, 2.37) * mm, "radius": 1 * mm});
            skCircle(sketch, "E47.9.10", {"center": v(0.92, 30.73) * mm, "radius": 1 * mm});
            skCircle(sketch, "E47.9.11", {"center": v(-35.06, 21.24) * mm, "radius": 1 * mm});
            skCircle(sketch, "E47.9.12", {"center": v(-25.4, 28.37) * mm, "radius": 1 * mm});
            skCircle(sketch, "E47.9.13", {"center": v(-30.5, 25.2) * mm, "radius": 1 * mm});
            skCircle(sketch, "E47.9.14", {"center": v(-32.83, 23.33) * mm, "radius": 1 * mm});
            skCircle(sketch, "E47.9.15", {"center": v(13.94, -10) * mm, "radius": 1 * mm});
            skCircle(sketch, "E47.9.16", {"center": v(-22.66, 29.6) * mm, "radius": 1 * mm});
            skCircle(sketch, "E47.9.17", {"center": v(-19.83, 30.6) * mm, "radius": 1 * mm});
            skCircle(sketch, "E47.9.18", {"center": v(-16.92, 31.33) * mm, "radius": 1 * mm});
            skCircle(sketch, "E47.9.19", {"center": v(-4.98, 31.8) * mm, "radius": 1 * mm});
            skCircle(sketch, "E47.9.20", {"center": v(21.47, 11.12) * mm, "radius": 1 * mm});
            skCircle(sketch, "E47.9.21", {"center": v(-10.97, 32.02) * mm, "radius": 1 * mm});
            skCircle(sketch, "E47.9.22", {"center": v(-7.97, 32.02) * mm, "radius": 1 * mm});
            skCircle(sketch, "E47.9.23", {"center": v(-5.36, -4.08) * mm, "radius": 1 * mm});
            skCircle(sketch, "E47.9.24", {"center": v(2.56, -12.23) * mm, "radius": 1 * mm});
            skCircle(sketch, "E47.9.25", {"center": v(3.8, 29.87) * mm, "radius": 1 * mm});
            skCircle(sketch, "E47.9.26", {"center": v(20.65, 14) * mm, "radius": 1 * mm});
            skCircle(sketch, "E47.9.27", {"center": v(14.14, 23.95) * mm, "radius": 1 * mm});
            skCircle(sketch, "E47.9.28", {"center": v(11.35, -11.5) * mm, "radius": 1 * mm});
            skCircle(sketch, "E47.9.29", {"center": v(8.5, -12.46) * mm, "radius": 1 * mm});
            skCircle(sketch, "E47.9.30", {"center": v(16.25, -8.08) * mm, "radius": 1 * mm});
            skCircle(sketch, "E47.9.31", {"center": v(22.02, 5.36) * mm, "radius": 1 * mm});
            skCircle(sketch, "E47.9.32", {"center": v(-28, 26.9) * mm, "radius": 1 * mm});
            skCircle(sketch, "E47.9.33", {"center": v(-2.65, -9.33) * mm, "radius": 1 * mm});
            skCircle(sketch, "E47.9.34", {"center": v(16.21, 21.78) * mm, "radius": 1 * mm});
            skCircle(sketch, "E47.9.35", {"center": v(21.92, 8.35) * mm, "radius": 1 * mm});
            skCircle(sketch, "E47.9.36", {"center": v(18.22, -5.82) * mm, "radius": 1 * mm});
            skCircle(sketch, "E47.9.37", {"center": v(9.28, 27.45) * mm, "radius": 1 * mm});
            skCircle(sketch, "E47.9.38", {"center": v(18, 19.37) * mm, "radius": 1 * mm});
            skCircle(sketch, "E47.9.39", {"center": v(-4.46, -6.94) * mm, "radius": 1 * mm});
            skCircle(sketch, "E47.9.40", {"center": v(11.82, 25.84) * mm, "radius": 1 * mm});
            skSolve(sketch);
        }
        {
            var Q0;
            Q0 = qSketchRegion(id + "F8", true);
            extrude(context, id + "F9", {"entities" : qUnion([Q0]), "operationType" : NewBodyOperationType.REMOVE, "oppositeDirection" : true, "depth" : 25 * mm});
        }
        {
            var Q0;
            Q0=makeQuery(id+"F1.opExtrude","CAP_FACE",FACE,{"disambiguationData":[OSD([sQuery(id+"F0.wireOp",EDGE,"E0")])],"isStart":false});
            var sketch = newSketch(context, id + "F10", { "sketchPlane" : qUnion([Q0])});
            skArc(sketch, "E48", {"start": v(42.51, -21.8) * mm, "mid": v(36.6, -15.04) * mm, "end": v(28.94, -10.38) * mm, "construction": true});
            skCircle(sketch, "E49", {"center": v(38.02, -16.31) * mm, "radius": 1 * mm});
            skCircle(sketch, "E50", {"center": v(35.95, -14.5) * mm, "radius": 1 * mm});
            skCircle(sketch, "E51", {"center": v(31.59, -11.64) * mm, "radius": 1 * mm});
            skCircle(sketch, "E52", {"center": v(29.92, -14.1) * mm, "radius": 1 * mm});
            skCircle(sketch, "E53", {"center": v(37.55, -12.17) * mm, "radius": 1 * mm});
            skCircle(sketch, "E54", {"center": v(33.18, -9.3) * mm, "radius": 1 * mm});
            skCircle(sketch, "E55", {"center": v(39.07, -9.6) * mm, "radius": 1 * mm});
            skCircle(sketch, "E56", {"center": v(34.7, -6.73) * mm, "radius": 1 * mm});
            skCircle(sketch, "E57", {"center": v(40.53, -7) * mm, "radius": 1 * mm});
            skCircle(sketch, "E58", {"center": v(36.17, -4.13) * mm, "radius": 1 * mm});
            skCircle(sketch, "E59", {"center": v(41.3, -4.07) * mm, "radius": 1 * mm});
            skCircle(sketch, "E60", {"center": v(36.93, -1.2) * mm, "radius": 1 * mm});
            skCircle(sketch, "E61", {"center": v(37.73, 2.32) * mm, "radius": 1 * mm});
            skCircle(sketch, "E62.2.0", {"center": v(38.3, 5.47) * mm, "radius": 1 * mm});
            skArc(sketch, "E63.1.0", {"start": v(47.2, 7.36) * mm, "mid": v(38.46, 9.34) * mm, "end": v(29.52, 8.62) * mm, "construction": true});
            skCircle(sketch, "E63.1.1", {"center": v(29.16, 24.06) * mm, "radius": 1 * mm});
            skCircle(sketch, "E63.1.2", {"center": v(27.77, 26.94) * mm, "radius": 1 * mm});
            skCircle(sketch, "E63.1.3", {"center": v(32.5, 6.19) * mm, "radius": 1 * mm});
            skCircle(sketch, "E63.1.4", {"center": v(37.53, 12.22) * mm, "radius": 1 * mm});
            skCircle(sketch, "E63.1.5", {"center": v(32.31, 11.98) * mm, "radius": 1 * mm});
            skCircle(sketch, "E63.1.6", {"center": v(37.25, 15.2) * mm, "radius": 1 * mm});
            skCircle(sketch, "E63.1.7", {"center": v(32.03, 14.96) * mm, "radius": 1 * mm});
            skCircle(sketch, "E63.1.8", {"center": v(36.9, 18.16) * mm, "radius": 1 * mm});
            skCircle(sketch, "E63.1.9", {"center": v(31.68, 17.92) * mm, "radius": 1 * mm});
            skCircle(sketch, "E63.1.10", {"center": v(37.61, 9.4) * mm, "radius": 1 * mm});
            skCircle(sketch, "E63.1.11", {"center": v(35.8, 20.98) * mm, "radius": 1 * mm});
            skCircle(sketch, "E63.1.12", {"center": v(40.34, 9.15) * mm, "radius": 1 * mm});
            skCircle(sketch, "E63.1.13", {"center": v(30.59, 20.74) * mm, "radius": 1 * mm});
            skCircle(sketch, "E63.1.14", {"center": v(32.4, 9.15) * mm, "radius": 1 * mm});
            skArc(sketch, "E63.2.0", {"start": v(33.86, 33.7) * mm, "mid": v(25.62, 30.16) * mm, "end": v(18.81, 24.32) * mm, "construction": true});
            skCircle(sketch, "E63.2.1", {"center": v(9.45, 36.6) * mm, "radius": 1 * mm});
            skCircle(sketch, "E63.2.2", {"center": v(6.63, 38.12) * mm, "radius": 1 * mm});
            skCircle(sketch, "E63.2.3", {"center": v(22.65, 24.1) * mm, "radius": 1 * mm});
            skCircle(sketch, "E63.2.4", {"center": v(23.18, 31.95) * mm, "radius": 1 * mm});
            skCircle(sketch, "E63.2.5", {"center": v(19.1, 28.69) * mm, "radius": 1 * mm});
            skCircle(sketch, "E63.2.6", {"center": v(21.2, 34.19) * mm, "radius": 1 * mm});
            skCircle(sketch, "E63.2.7", {"center": v(17.13, 30.93) * mm, "radius": 1 * mm});
            skCircle(sketch, "E63.2.8", {"center": v(19.18, 36.38) * mm, "radius": 1 * mm});
            skCircle(sketch, "E63.2.9", {"center": v(15.1, 33.12) * mm, "radius": 1 * mm});
            skCircle(sketch, "E63.2.10", {"center": v(24.9, 29.7) * mm, "radius": 1 * mm});
            skCircle(sketch, "E63.2.11", {"center": v(16.63, 38.02) * mm, "radius": 1 * mm});
            skCircle(sketch, "E63.2.12", {"center": v(27.26, 31.12) * mm, "radius": 1 * mm});
            skCircle(sketch, "E63.2.13", {"center": v(12.55, 34.76) * mm, "radius": 1 * mm});
            skCircle(sketch, "E63.2.14", {"center": v(20.83, 26.44) * mm, "radius": 1 * mm});
            skArc(sketch, "E63.3.0", {"start": v(7.59, 47.17) * mm, "mid": v(3, 39.46) * mm, "end": v(0.92, 30.73) * mm, "construction": true});
            skCircle(sketch, "E63.3.1", {"center": v(-13.87, 35.17) * mm, "radius": 1 * mm});
            skCircle(sketch, "E63.3.2", {"center": v(-17.04, 34.74) * mm, "radius": 1 * mm});
            skCircle(sketch, "E63.3.3", {"center": v(4.16, 32.81) * mm, "radius": 1 * mm});
            skCircle(sketch, "E63.3.4", {"center": v(-0.03, 39.47) * mm, "radius": 1 * mm});
            skCircle(sketch, "E63.3.5", {"center": v(-1.41, 34.43) * mm, "radius": 1 * mm});
            skCircle(sketch, "E63.3.6", {"center": v(-2.94, 40.12) * mm, "radius": 1 * mm});
            skCircle(sketch, "E63.3.7", {"center": v(-4.32, 35.09) * mm, "radius": 1 * mm});
            skCircle(sketch, "E63.3.8", {"center": v(-5.87, 40.7) * mm, "radius": 1 * mm});
            skCircle(sketch, "E63.3.9", {"center": v(-7.25, 35.67) * mm, "radius": 1 * mm});
            skCircle(sketch, "E63.3.10", {"center": v(2.69, 38.67) * mm, "radius": 1 * mm});
            skCircle(sketch, "E63.3.11", {"center": v(-8.89, 40.53) * mm, "radius": 1 * mm});
            skCircle(sketch, "E63.3.12", {"center": v(3.77, 41.2) * mm, "radius": 1 * mm});
            skCircle(sketch, "E63.3.13", {"center": v(-10.27, 35.5) * mm, "radius": 1 * mm});
            skCircle(sketch, "E63.3.14", {"center": v(1.3, 33.64) * mm, "radius": 1 * mm});
            skArc(sketch, "E63.4.0", {"start": v(-21.59, 42.62) * mm, "mid": v(-20.77, 33.69) * mm, "end": v(-17.32, 25.4) * mm, "construction": true});
            skCircle(sketch, "E63.4.1", {"center": v(-31.89, 20.3) * mm, "radius": 1 * mm});
            skCircle(sketch, "E63.4.2", {"center": v(-34.2, 18.09) * mm, "radius": 1 * mm});
            skCircle(sketch, "E63.4.3", {"center": v(-15.92, 29) * mm, "radius": 1 * mm});
            skCircle(sketch, "E63.4.4", {"center": v(-23.22, 31.91) * mm, "radius": 1 * mm});
            skCircle(sketch, "E63.4.5", {"center": v(-21.38, 27.03) * mm, "radius": 1 * mm});
            skCircle(sketch, "E63.4.6", {"center": v(-25.96, 30.73) * mm, "radius": 1 * mm});
            skCircle(sketch, "E63.4.7", {"center": v(-24.12, 25.85) * mm, "radius": 1 * mm});
            skCircle(sketch, "E63.4.8", {"center": v(-28.68, 29.48) * mm, "radius": 1 * mm});
            skCircle(sketch, "E63.4.9", {"center": v(-26.83, 24.6) * mm, "radius": 1 * mm});
            skCircle(sketch, "E63.4.10", {"center": v(-20.55, 32.87) * mm, "radius": 1 * mm});
            skCircle(sketch, "E63.4.11", {"center": v(-31.02, 27.57) * mm, "radius": 1 * mm});
            skCircle(sketch, "E63.4.12", {"center": v(-21.17, 35.54) * mm, "radius": 1 * mm});
            skCircle(sketch, "E63.4.13", {"center": v(-29.17, 22.68) * mm, "radius": 1 * mm});
            skCircle(sketch, "E63.4.14", {"center": v(-18.71, 27.98) * mm, "radius": 1 * mm});
            skArc(sketch, "E63.5.0", {"start": v(-42.51, 21.8) * mm, "mid": v(-36.6, 15.04) * mm, "end": v(-28.94, 10.38) * mm, "construction": true});
            skCircle(sketch, "E63.5.1", {"center": v(-37.73, -2.32) * mm, "radius": 1 * mm});
            skCircle(sketch, "E63.5.2", {"center": v(-38.3, -5.47) * mm, "radius": 1 * mm});
            skCircle(sketch, "E63.5.3", {"center": v(-29.92, 14.1) * mm, "radius": 1 * mm});
            skCircle(sketch, "E63.5.4", {"center": v(-37.55, 12.17) * mm, "radius": 1 * mm});
            skCircle(sketch, "E63.5.5", {"center": v(-33.18, 9.3) * mm, "radius": 1 * mm});
            skCircle(sketch, "E63.5.6", {"center": v(-39.07, 9.6) * mm, "radius": 1 * mm});
            skCircle(sketch, "E63.5.7", {"center": v(-34.7, 6.73) * mm, "radius": 1 * mm});
            skCircle(sketch, "E63.5.8", {"center": v(-40.53, 7) * mm, "radius": 1 * mm});
            skCircle(sketch, "E63.5.9", {"center": v(-36.17, 4.13) * mm, "radius": 1 * mm});
            skCircle(sketch, "E63.5.10", {"center": v(-35.95, 14.5) * mm, "radius": 1 * mm});
            skCircle(sketch, "E63.5.11", {"center": v(-41.3, 4.07) * mm, "radius": 1 * mm});
            skCircle(sketch, "E63.5.12", {"center": v(-38.02, 16.31) * mm, "radius": 1 * mm});
            skCircle(sketch, "E63.5.13", {"center": v(-36.93, 1.2) * mm, "radius": 1 * mm});
            skCircle(sketch, "E63.5.14", {"center": v(-31.59, 11.64) * mm, "radius": 1 * mm});
            skArc(sketch, "E63.6.0", {"start": v(-47.2, -7.36) * mm, "mid": v(-38.46, -9.34) * mm, "end": v(-29.52, -8.62) * mm, "construction": true});
            skCircle(sketch, "E63.6.1", {"center": v(-29.16, -24.06) * mm, "radius": 1 * mm});
            skCircle(sketch, "E63.6.2", {"center": v(-27.77, -26.94) * mm, "radius": 1 * mm});
            skCircle(sketch, "E63.6.3", {"center": v(-32.5, -6.19) * mm, "radius": 1 * mm});
            skCircle(sketch, "E63.6.4", {"center": v(-37.53, -12.22) * mm, "radius": 1 * mm});
            skCircle(sketch, "E63.6.5", {"center": v(-32.31, -11.98) * mm, "radius": 1 * mm});
            skCircle(sketch, "E63.6.6", {"center": v(-37.25, -15.2) * mm, "radius": 1 * mm});
            skCircle(sketch, "E63.6.7", {"center": v(-32.03, -14.96) * mm, "radius": 1 * mm});
            skCircle(sketch, "E63.6.8", {"center": v(-36.9, -18.16) * mm, "radius": 1 * mm});
            skCircle(sketch, "E63.6.9", {"center": v(-31.68, -17.92) * mm, "radius": 1 * mm});
            skCircle(sketch, "E63.6.10", {"center": v(-37.61, -9.4) * mm, "radius": 1 * mm});
            skCircle(sketch, "E63.6.11", {"center": v(-35.8, -20.98) * mm, "radius": 1 * mm});
            skCircle(sketch, "E63.6.12", {"center": v(-40.34, -9.15) * mm, "radius": 1 * mm});
            skCircle(sketch, "E63.6.13", {"center": v(-30.59, -20.74) * mm, "radius": 1 * mm});
            skCircle(sketch, "E63.6.14", {"center": v(-32.4, -9.15) * mm, "radius": 1 * mm});
            skArc(sketch, "E63.7.0", {"start": v(-33.86, -33.7) * mm, "mid": v(-25.62, -30.16) * mm, "end": v(-18.81, -24.32) * mm, "construction": true});
            skCircle(sketch, "E63.7.1", {"center": v(-9.45, -36.6) * mm, "radius": 1 * mm});
            skCircle(sketch, "E63.7.2", {"center": v(-6.63, -38.12) * mm, "radius": 1 * mm});
            skCircle(sketch, "E63.7.3", {"center": v(-22.65, -24.1) * mm, "radius": 1 * mm});
            skCircle(sketch, "E63.7.4", {"center": v(-23.18, -31.95) * mm, "radius": 1 * mm});
            skCircle(sketch, "E63.7.5", {"center": v(-19.1, -28.69) * mm, "radius": 1 * mm});
            skCircle(sketch, "E63.7.6", {"center": v(-21.2, -34.19) * mm, "radius": 1 * mm});
            skCircle(sketch, "E63.7.7", {"center": v(-17.13, -30.93) * mm, "radius": 1 * mm});
            skCircle(sketch, "E63.7.8", {"center": v(-19.18, -36.38) * mm, "radius": 1 * mm});
            skCircle(sketch, "E63.7.9", {"center": v(-15.1, -33.12) * mm, "radius": 1 * mm});
            skCircle(sketch, "E63.7.10", {"center": v(-24.9, -29.7) * mm, "radius": 1 * mm});
            skCircle(sketch, "E63.7.11", {"center": v(-16.63, -38.02) * mm, "radius": 1 * mm});
            skCircle(sketch, "E63.7.12", {"center": v(-27.26, -31.12) * mm, "radius": 1 * mm});
            skCircle(sketch, "E63.7.13", {"center": v(-12.55, -34.76) * mm, "radius": 1 * mm});
            skCircle(sketch, "E63.7.14", {"center": v(-20.83, -26.44) * mm, "radius": 1 * mm});
            skArc(sketch, "E63.8.0", {"start": v(-7.59, -47.17) * mm, "mid": v(-3, -39.46) * mm, "end": v(-0.92, -30.73) * mm, "construction": true});
            skCircle(sketch, "E63.8.1", {"center": v(13.87, -35.17) * mm, "radius": 1 * mm});
            skCircle(sketch, "E63.8.2", {"center": v(17.04, -34.74) * mm, "radius": 1 * mm});
            skCircle(sketch, "E63.8.3", {"center": v(-4.16, -32.81) * mm, "radius": 1 * mm});
            skCircle(sketch, "E63.8.4", {"center": v(0.03, -39.47) * mm, "radius": 1 * mm});
            skCircle(sketch, "E63.8.5", {"center": v(1.41, -34.43) * mm, "radius": 1 * mm});
            skCircle(sketch, "E63.8.6", {"center": v(2.94, -40.12) * mm, "radius": 1 * mm});
            skCircle(sketch, "E63.8.7", {"center": v(4.32, -35.09) * mm, "radius": 1 * mm});
            skCircle(sketch, "E63.8.8", {"center": v(5.87, -40.7) * mm, "radius": 1 * mm});
            skCircle(sketch, "E63.8.9", {"center": v(7.25, -35.67) * mm, "radius": 1 * mm});
            skCircle(sketch, "E63.8.10", {"center": v(-2.69, -38.67) * mm, "radius": 1 * mm});
            skCircle(sketch, "E63.8.11", {"center": v(8.89, -40.53) * mm, "radius": 1 * mm});
            skCircle(sketch, "E63.8.12", {"center": v(-3.77, -41.2) * mm, "radius": 1 * mm});
            skCircle(sketch, "E63.8.13", {"center": v(10.27, -35.5) * mm, "radius": 1 * mm});
            skCircle(sketch, "E63.8.14", {"center": v(-1.3, -33.64) * mm, "radius": 1 * mm});
            skArc(sketch, "E63.9.0", {"start": v(21.59, -42.62) * mm, "mid": v(20.77, -33.69) * mm, "end": v(17.32, -25.4) * mm, "construction": true});
            skCircle(sketch, "E63.9.1", {"center": v(31.89, -20.3) * mm, "radius": 1 * mm});
            skCircle(sketch, "E63.9.2", {"center": v(34.2, -18.09) * mm, "radius": 1 * mm});
            skCircle(sketch, "E63.9.3", {"center": v(15.92, -29) * mm, "radius": 1 * mm});
            skCircle(sketch, "E63.9.4", {"center": v(23.22, -31.91) * mm, "radius": 1 * mm});
            skCircle(sketch, "E63.9.5", {"center": v(21.38, -27.03) * mm, "radius": 1 * mm});
            skCircle(sketch, "E63.9.6", {"center": v(25.96, -30.73) * mm, "radius": 1 * mm});
            skCircle(sketch, "E63.9.7", {"center": v(24.12, -25.85) * mm, "radius": 1 * mm});
            skCircle(sketch, "E63.9.8", {"center": v(28.68, -29.48) * mm, "radius": 1 * mm});
            skCircle(sketch, "E63.9.9", {"center": v(26.83, -24.6) * mm, "radius": 1 * mm});
            skCircle(sketch, "E63.9.10", {"center": v(20.55, -32.87) * mm, "radius": 1 * mm});
            skCircle(sketch, "E63.9.11", {"center": v(31.02, -27.57) * mm, "radius": 1 * mm});
            skCircle(sketch, "E63.9.12", {"center": v(21.17, -35.54) * mm, "radius": 1 * mm});
            skCircle(sketch, "E63.9.13", {"center": v(29.17, -22.68) * mm, "radius": 1 * mm});
            skCircle(sketch, "E63.9.14", {"center": v(18.71, -27.98) * mm, "radius": 1 * mm});
            skPoint(sketch, "E63.center", {"position": v(0, 0) * mm});
            skCircle(sketch, "E64", {"center": v(3.14, 0) * mm, "radius": 1.5 * mm});
            skCircle(sketch, "E65.1.0", {"center": v(-1.57, 2.72) * mm, "radius": 1.5 * mm});
            skCircle(sketch, "E65.2.0", {"center": v(-1.57, -2.72) * mm, "radius": 1.5 * mm});
            skSolve(sketch);
        }
        {
            var Q0;
            Q0 = qSketchRegion(id + "F10", true);
            extrude(context, id + "F11", {"entities" : qUnion([Q0]), "operationType" : NewBodyOperationType.REMOVE, "oppositeDirection" : true, "depth" : 25 * mm});
        }
    });
